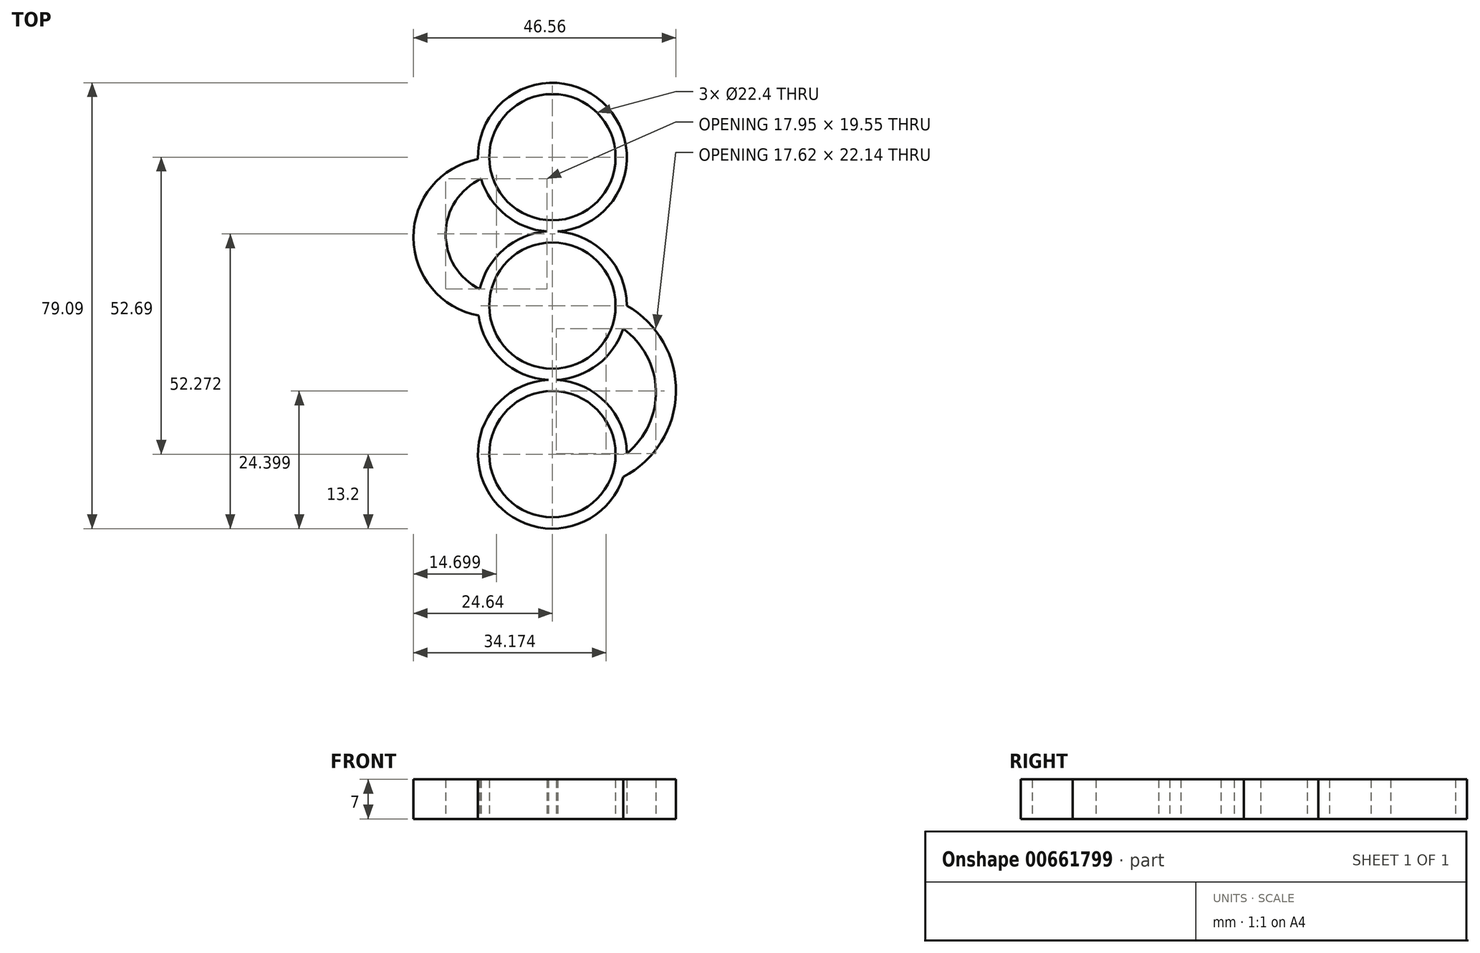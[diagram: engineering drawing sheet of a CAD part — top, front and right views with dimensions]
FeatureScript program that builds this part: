
annotation { "Feature Type Name" : "Feature", "Feature Type Description" : "" }
export const myFeature = defineFeature(function(context is Context, id is Id, definition is map)
    precondition{}
    {
        {
            var Q0;
            Q0=qCreatedBy(makeId("Top.planeOp"),FACE);
            var sketch = newSketch(context, id + "F0", { "sketchPlane" : qUnion([Q0])});
            skCircle(sketch, "E0", {"center": v(0, 0) * mm, "radius": 11.2 * mm});
            skCircle(sketch, "E1", {"center": v(0, 0) * mm, "radius": 13.2 * mm});
            skCircle(sketch, "E2", {"center": v(0, 26.33) * mm, "radius": 11.2 * mm});
            skCircle(sketch, "E3", {"center": v(0, 26.33) * mm, "radius": 13.2 * mm});
            skCircle(sketch, "E4", {"center": v(0, -26.36) * mm, "radius": 11.2 * mm});
            skCircle(sketch, "E5", {"center": v(0, -26.36) * mm, "radius": 13.2 * mm});
            skArc(sketch, "E6", {"start": v(-12.63, 22.49) * mm, "mid": v(-18.92, 12.79) * mm, "end": v(-12.87, 2.94) * mm});
            skArc(sketch, "E7", {"start": v(-13.2, 26) * mm, "mid": v(-24.64, 12.08) * mm, "end": v(-13.08, -1.76) * mm});
            skArc(sketch, "E8", {"start": v(13.2, -26.23) * mm, "mid": v(18.35, -15) * mm, "end": v(12.55, -4.1) * mm});
            skArc(sketch, "E9", {"start": v(12.57, -30.4) * mm, "mid": v(21.91, -15.39) * mm, "end": v(13.2, 0) * mm});
            skSolve(sketch);
        }
        {
            var Q0;
            Q0 = qSketchRegion(id + "F0", true);
            extrude(context, id + "F1", {"entities" : qUnion([Q0]), "depth" : 7 * mm, "offsetDistance" : 25 * mm});
        }
    });
